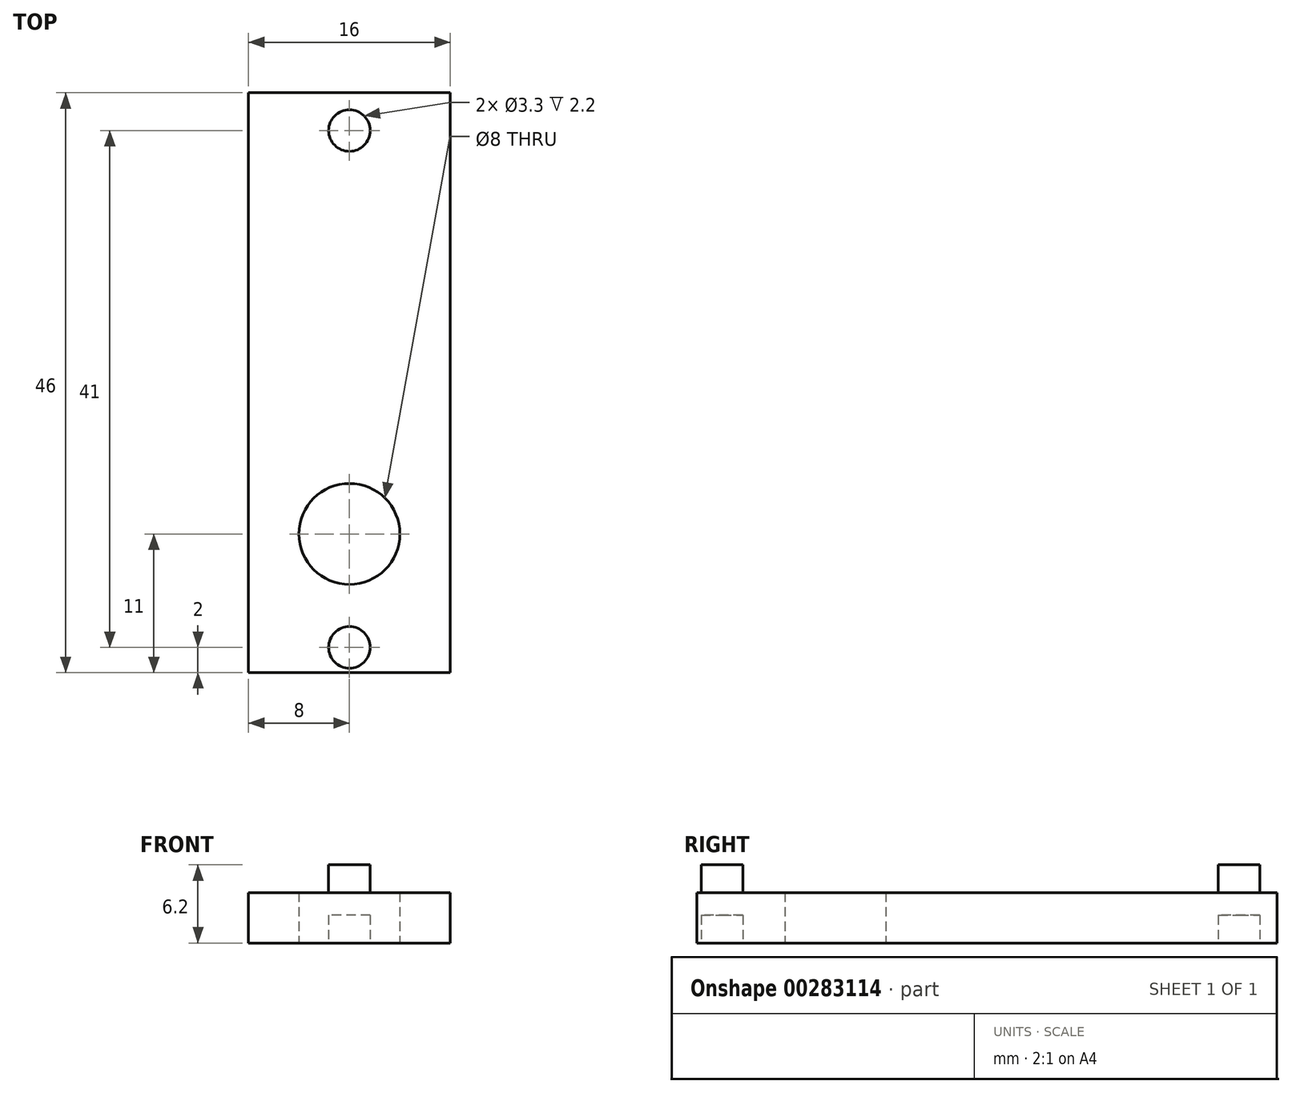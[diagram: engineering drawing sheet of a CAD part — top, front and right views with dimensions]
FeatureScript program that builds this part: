
annotation { "Feature Type Name" : "Feature", "Feature Type Description" : "" }
export const myFeature = defineFeature(function(context is Context, id is Id, definition is map)
    precondition{}
    {
        {
            var Q0;
            Q0=qCreatedBy(makeId("Top.planeOp"),FACE);
            var sketch = newSketch(context, id + "F0", { "sketchPlane" : qUnion([Q0])});
            skLineSegment(sketch, "E0.bottom", {"start": v(-8, 23) * mm, "end": v(8, 23) * mm});
            skLineSegment(sketch, "E0.top", {"start": v(-8, -23) * mm, "end": v(8, -23) * mm});
            skLineSegment(sketch, "E0.left", {"start": v(-8, 23) * mm, "end": v(-8, -23) * mm});
            skLineSegment(sketch, "E0.right", {"start": v(8, 23) * mm, "end": v(8, -23) * mm});
            skPoint(sketch, "E0.middle", {"position": v(0, 0) * mm});
            skCircle(sketch, "E1", {"center": v(0, -21) * mm, "radius": 1.65 * mm});
            skCircle(sketch, "E2.0.1.0", {"center": v(0, 20) * mm, "radius": 1.65 * mm});
            skLineSegment(sketch, "E2.direction1", {"start": v(0, -21) * mm, "end": v(25, -21) * mm, "construction": true});
            skLineSegment(sketch, "E2.direction2", {"start": v(0, -21) * mm, "end": v(0, 20) * mm, "construction": true});
            skCircle(sketch, "E3", {"center": v(0, -12) * mm, "radius": 4 * mm});
            skSolve(sketch);
        }
        {
            var Q0;
            Q0=makeQuery(id+"F0.imprint","IMPRINT",FACE,{"disambiguationData":[TD([[makeQuery(id+"F0.imprint","IMPRINT",EDGE,{"derivedFrom":sQuery(id+"F0.wireOp",EDGE,"E0.bottom")}),-1.0]])]});
            var Q1;
            Q1=makeQuery(id+"F0.imprint","IMPRINT",FACE,{"disambiguationData":[TD([[makeQuery(id+"F0.imprint","IMPRINT",EDGE,{"derivedFrom":sQuery(id+"F0.wireOp",EDGE,"E2.0.1.0")}),1.0]])]});
            var Q2;
            Q2=makeQuery(id+"F0.imprint","IMPRINT",FACE,{"disambiguationData":[TD([[makeQuery(id+"F0.imprint","IMPRINT",EDGE,{"derivedFrom":sQuery(id+"F0.wireOp",EDGE,"E1")}),1.0]])]});
            extrude(context, id + "F1", {"entities" : qUnion([Q0, Q1, Q2]), "depth" : 4 * mm});
        }
        {
            var Q0;
            Q0=makeQuery(id+"F0.imprint","IMPRINT",FACE,{"disambiguationData":[TD([[makeQuery(id+"F0.imprint","IMPRINT",EDGE,{"derivedFrom":sQuery(id+"F0.wireOp",EDGE,"E2.0.1.0")}),1.0]])]});
            var Q1;
            Q1=makeQuery(id+"F0.imprint","IMPRINT",FACE,{"disambiguationData":[TD([[makeQuery(id+"F0.imprint","IMPRINT",EDGE,{"derivedFrom":sQuery(id+"F0.wireOp",EDGE,"E1")}),1.0]])]});
            extrude(context, id + "F2", {"entities" : qUnion([Q0, Q1]), "operationType" : NewBodyOperationType.ADD, "depth" : 6.2 * mm});
        }
        {
            var Q0;
            Q0=makeQuery(id+"F0.imprint","IMPRINT",FACE,{"disambiguationData":[TD([[makeQuery(id+"F0.imprint","IMPRINT",EDGE,{"derivedFrom":sQuery(id+"F0.wireOp",EDGE,"E1")}),1.0]])]});
            var Q1;
            Q1=makeQuery(id+"F0.imprint","IMPRINT",FACE,{"disambiguationData":[TD([[makeQuery(id+"F0.imprint","IMPRINT",EDGE,{"derivedFrom":sQuery(id+"F0.wireOp",EDGE,"E2.0.1.0")}),1.0]])]});
            extrude(context, id + "F3", {"entities" : qUnion([Q0, Q1]), "operationType" : NewBodyOperationType.REMOVE, "depth" : 2.2 * mm});
        }
    });
